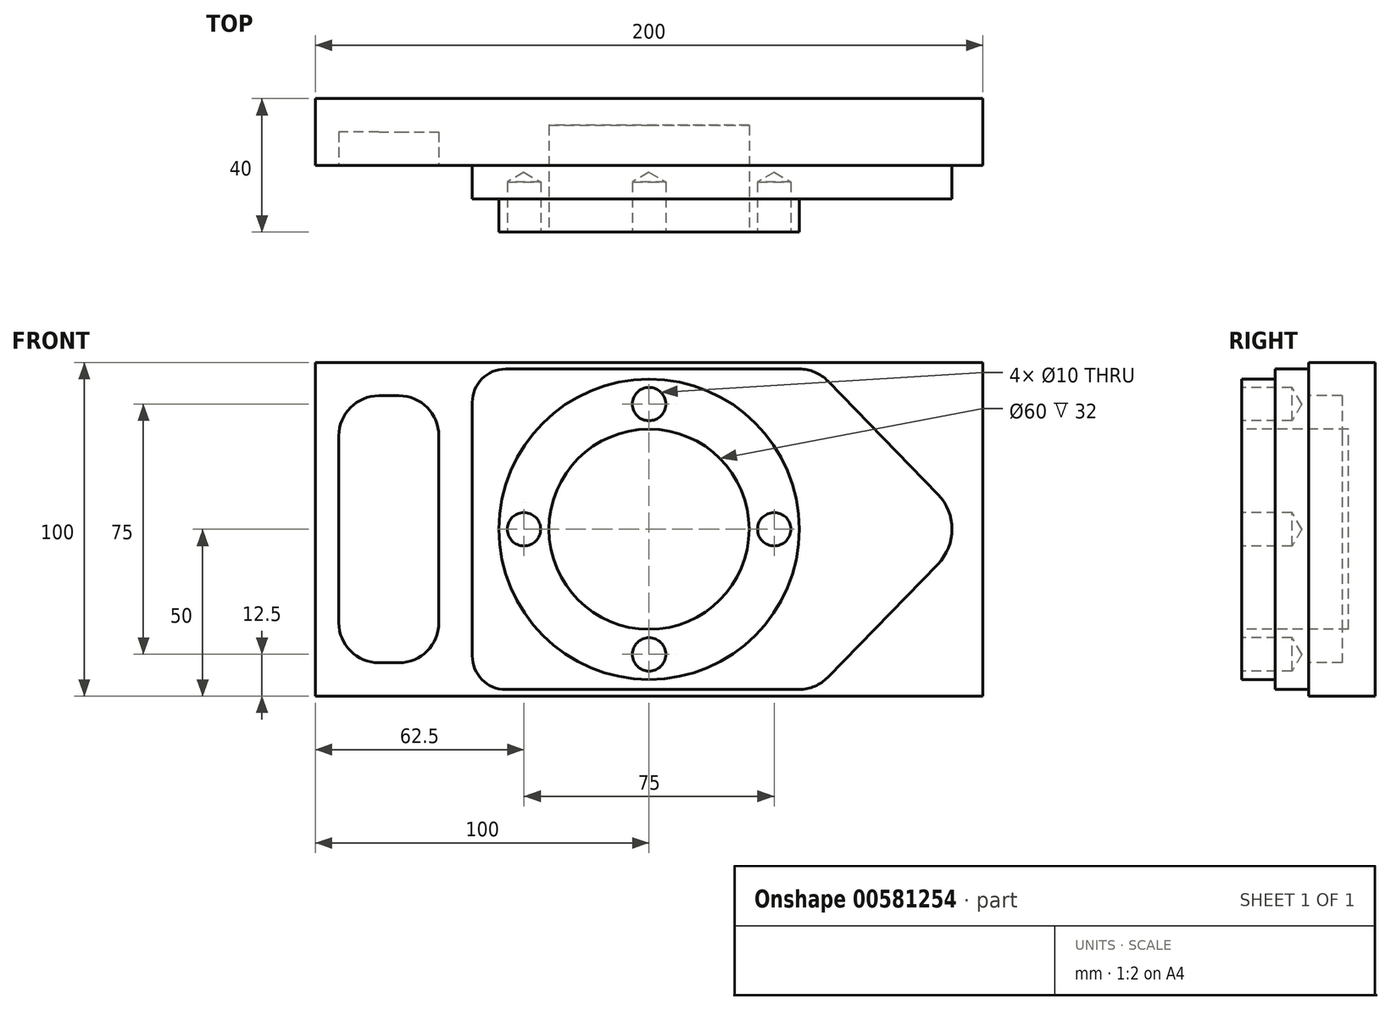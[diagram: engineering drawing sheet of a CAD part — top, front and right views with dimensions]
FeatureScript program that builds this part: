
annotation { "Feature Type Name" : "Feature", "Feature Type Description" : "" }
export const myFeature = defineFeature(function(context is Context, id is Id, definition is map)
    precondition{}
    {
        {
            var Q0;
            Q0=qCreatedBy(makeId("Front.planeOp"),FACE);
            var sketch = newSketch(context, id + "F0", { "sketchPlane" : qUnion([Q0])});
            skLineSegment(sketch, "E0.bottom", {"start": v(-100, 50) * mm, "end": v(100, 50) * mm});
            skLineSegment(sketch, "E0.top", {"start": v(-100, -50) * mm, "end": v(100, -50) * mm});
            skLineSegment(sketch, "E0.left", {"start": v(-100, 50) * mm, "end": v(-100, -50) * mm});
            skLineSegment(sketch, "E0.right", {"start": v(100, 50) * mm, "end": v(100, -50) * mm});
            skPoint(sketch, "E0.middle", {"position": v(0, 0) * mm});
            skSolve(sketch);
        }
        {
            var Q0;
            Q0=makeQuery(id+"F0.imprint","IMPRINT",FACE,{"disambiguationData":[TD([[makeQuery(id+"F0.imprint","IMPRINT",EDGE,{"derivedFrom":sQuery(id+"F0.wireOp",EDGE,"E0.bottom")}),-1.0]])]});
            extrude(context, id + "F1", {"entities" : qUnion([Q0]), "depth" : 20 * mm, "offsetDistance" : 25 * mm});
        }
        {
            var Q0;
            Q0=makeQuery(id+"F1.opExtrude","CAP_FACE",FACE,{"disambiguationData":[OSD([sQuery(id+"F0.wireOp",EDGE,"E0.bottom"),sQuery(id+"F0.wireOp",EDGE,"E0.top"),sQuery(id+"F0.wireOp",EDGE,"E0.left"),sQuery(id+"F0.wireOp",EDGE,"E0.right")])],"isStart":false});
            var sketch = newSketch(context, id + "F2", { "sketchPlane" : qUnion([Q0])});
            skLineSegment(sketch, "E1.bottom", {"start": v(-81, 40) * mm, "end": v(-75, 40) * mm});
            skLineSegment(sketch, "E1.top", {"start": v(-81, -40) * mm, "end": v(-75, -40) * mm});
            skLineSegment(sketch, "E1.left", {"start": v(-93, 28) * mm, "end": v(-93, -28) * mm});
            skLineSegment(sketch, "E1.right", {"start": v(-63, 28) * mm, "end": v(-63, -28) * mm});
            skPoint(sketch, "E2.visualSharp", {"position": v(-93, 40) * mm});
            skArc(sketch, "E2.filletArc", {"start": v(-81, 40) * mm, "mid": v(-89.49, 36.49) * mm, "end": v(-93, 28) * mm});
            skPoint(sketch, "E3.visualSharp", {"position": v(-63, 40) * mm});
            skArc(sketch, "E3.filletArc", {"start": v(-63, 28) * mm, "mid": v(-66.51, 36.49) * mm, "end": v(-75, 40) * mm});
            skPoint(sketch, "E4.visualSharp", {"position": v(-93, -40) * mm});
            skArc(sketch, "E4.filletArc", {"start": v(-93, -28) * mm, "mid": v(-89.49, -36.49) * mm, "end": v(-81, -40) * mm});
            skPoint(sketch, "E5.visualSharp", {"position": v(-63, -40) * mm});
            skArc(sketch, "E5.filletArc", {"start": v(-75, -40) * mm, "mid": v(-66.51, -36.49) * mm, "end": v(-63, -28) * mm});
            skSolve(sketch);
        }
        {
            var Q0;
            Q0=makeQuery(id+"F2.imprint","IMPRINT",FACE,{"disambiguationData":[TD([[makeQuery(id+"F2.imprint","IMPRINT",EDGE,{"derivedFrom":sQuery(id+"F2.wireOp",EDGE,"E1.bottom")}),-1.0]])]});
            var Q1;
            Q1 = qSketchRegion(id + "F4", true);
            extrude(context, id + "F3", {"entities" : qUnion([Q0, Q1]), "operationType" : NewBodyOperationType.REMOVE, "oppositeDirection" : true, "depth" : 10 * mm, "offsetDistance" : 25 * mm});
        }
        {
            var Q0;
            Q0=makeQuery(id+"F1.opExtrude","CAP_FACE",FACE,{"disambiguationData":[OSD([sQuery(id+"F0.wireOp",EDGE,"E0.bottom"),sQuery(id+"F0.wireOp",EDGE,"E0.top"),sQuery(id+"F0.wireOp",EDGE,"E0.left"),sQuery(id+"F0.wireOp",EDGE,"E0.right")])],"isStart":false});
            var sketch = newSketch(context, id + "F4", { "sketchPlane" : qUnion([Q0])});
            skLineSegment(sketch, "E6.bottom", {"start": v(-43, 48) * mm, "end": v(45.03, 48) * mm});
            skLineSegment(sketch, "E6.top", {"start": v(-43, -48) * mm, "end": v(45.03, -48) * mm});
            skLineSegment(sketch, "E6.left", {"start": v(-53, 38) * mm, "end": v(-53, -38) * mm});
            skPoint(sketch, "E6.middle", {"position": v(0, 0) * mm});
            skLineSegment(sketch, "E7", {"start": v(53.64, 44.36) * mm, "end": v(86.55, 10.45) * mm});
            skLineSegment(sketch, "E8", {"start": v(53.51, -44.37) * mm, "end": v(86.53, -10.46) * mm});
            skPoint(sketch, "E9.visualSharp", {"position": v(-53, 48) * mm});
            skArc(sketch, "E9.filletArc", {"start": v(-43, 48) * mm, "mid": v(-50.07, 45.07) * mm, "end": v(-53, 38) * mm});
            skPoint(sketch, "E10.visualSharp", {"position": v(-53, -48) * mm});
            skArc(sketch, "E10.filletArc", {"start": v(-53, -38) * mm, "mid": v(-50.07, -45.07) * mm, "end": v(-43, -48) * mm});
            skArc(sketch, "E11", {"start": v(53.64, 44.36) * mm, "mid": v(49.7, 47.05) * mm, "end": v(45.03, 48) * mm});
            skArc(sketch, "E12", {"start": v(45.03, -48) * mm, "mid": v(49.63, -47.03) * mm, "end": v(53.51, -44.37) * mm});
            skArc(sketch, "E13", {"start": v(86.53, -10.46) * mm, "mid": v(90.78, -0.01) * mm, "end": v(86.55, 10.45) * mm});
            skSolve(sketch);
        }
        {
            var Q0;
            Q0=makeQuery(id+"F4.imprint","IMPRINT",FACE,{"disambiguationData":[TD([[makeQuery(id+"F4.imprint","IMPRINT",EDGE,{"derivedFrom":sQuery(id+"F4.wireOp",EDGE,"E6.bottom")}),-1.0]])]});
            extrude(context, id + "F5", {"entities" : qUnion([Q0]), "operationType" : NewBodyOperationType.ADD, "depth" : 10 * mm, "offsetDistance" : 25 * mm});
        }
        {
            var Q0;
            Q0=makeQuery(id+"F5.opExtrude","CAP_FACE",FACE,{"disambiguationData":[OSD([sQuery(id+"F4.wireOp",EDGE,"E6.bottom"),sQuery(id+"F4.wireOp",EDGE,"E6.top"),sQuery(id+"F4.wireOp",EDGE,"E6.left"),sQuery(id+"F4.wireOp",EDGE,"E7"),sQuery(id+"F4.wireOp",EDGE,"E8"),sQuery(id+"F4.wireOp",EDGE,"E9.filletArc"),sQuery(id+"F4.wireOp",EDGE,"E10.filletArc"),sQuery(id+"F4.wireOp",EDGE,"E11"),sQuery(id+"F4.wireOp",EDGE,"E12"),sQuery(id+"F4.wireOp",EDGE,"E13")])],"isStart":false});
            var sketch = newSketch(context, id + "F6", { "sketchPlane" : qUnion([Q0])});
            skCircle(sketch, "E14", {"center": v(0, 0) * mm, "radius": 45 * mm});
            skSolve(sketch);
        }
        {
            var Q0;
            Q0=makeQuery(id+"F6.imprint","IMPRINT",FACE,{"disambiguationData":[TD([[makeQuery(id+"F6.imprint","IMPRINT",EDGE,{"derivedFrom":sQuery(id+"F6.wireOp",EDGE,"E14")}),1.0]])]});
            extrude(context, id + "F7", {"entities" : qUnion([Q0]), "operationType" : NewBodyOperationType.ADD, "depth" : 10 * mm, "offsetDistance" : 25 * mm});
        }
        {
            var Q0;
            Q0=makeQuery(id+"F7.opExtrude","CAP_FACE",FACE,{"disambiguationData":[OSD([sQuery(id+"F6.wireOp",EDGE,"E14")])],"isStart":false});
            var sketch = newSketch(context, id + "F8", { "sketchPlane" : qUnion([Q0])});
            skCircle(sketch, "E15", {"center": v(0, 0) * mm, "radius": 30 * mm});
            skSolve(sketch);
        }
        {
            var Q0;
            Q0=makeQuery(id+"F8.imprint","IMPRINT",FACE,{"disambiguationData":[TD([[makeQuery(id+"F8.imprint","IMPRINT",EDGE,{"derivedFrom":sQuery(id+"F8.wireOp",EDGE,"E15")}),1.0]])]});
            extrude(context, id + "F9", {"entities" : qUnion([Q0]), "operationType" : NewBodyOperationType.REMOVE, "oppositeDirection" : true, "depth" : 32 * mm, "offsetDistance" : 25 * mm});
        }
        {
            var Q0;
            Q0=makeQuery(id+"F7.opExtrude","CAP_FACE",FACE,{"disambiguationData":[OSD([sQuery(id+"F6.wireOp",EDGE,"E14")])],"isStart":false});
            var sketch = newSketch(context, id + "F10", { "sketchPlane" : qUnion([Q0])});
            skCircle(sketch, "E16", {"center": v(0, 0) * mm, "radius": 37.5 * mm, "construction": true});
            skCircle(sketch, "E17", {"center": v(-37.5, 0) * mm, "radius": 5 * mm});
            skCircle(sketch, "E18", {"center": v(0, 37.5) * mm, "radius": 5 * mm});
            skCircle(sketch, "E19", {"center": v(0, -37.5) * mm, "radius": 5 * mm});
            skCircle(sketch, "E20", {"center": v(37.5, 0) * mm, "radius": 5 * mm});
            skSolve(sketch);
        }
        {
            var Q0;
            Q0=sQuery(id+"F10.wireOp",VERTEX,"E17.center");
            var Q1;
            Q1=sQuery(id+"F10.wireOp",VERTEX,"E18.center");
            var Q2;
            Q2=sQuery(id+"F10.wireOp",VERTEX,"E20.center");
            var Q3;
            Q3=sQuery(id+"F10.wireOp",VERTEX,"E19.center");
            var Q4;
            Q4=makeQuery(id+"F1.opExtrude","SWEPT_BODY",BODY,{"disambiguationData":[OSD([sQuery(id+"F0.wireOp",EDGE,"E0.bottom"),sQuery(id+"F0.wireOp",EDGE,"E0.top"),sQuery(id+"F0.wireOp",EDGE,"E0.left"),sQuery(id+"F0.wireOp",EDGE,"E0.right")])]});
            hole(context, id + "F11", {"style" : HoleStyle.SIMPLE, "endStyle" : HoleEndStyle.BLIND, "holeDiameter" : 10 * mm, "majorDiameter" : 5 * mm, "holeDepth" : 15 * mm, "isTappedThrough" : true, "tappedDepth" : 12 * mm, "tapClearance" : 3, "locations" : qUnion([Q0, Q1, Q2, Q3]), "scope" : qUnion([Q4])});
        }
    });
